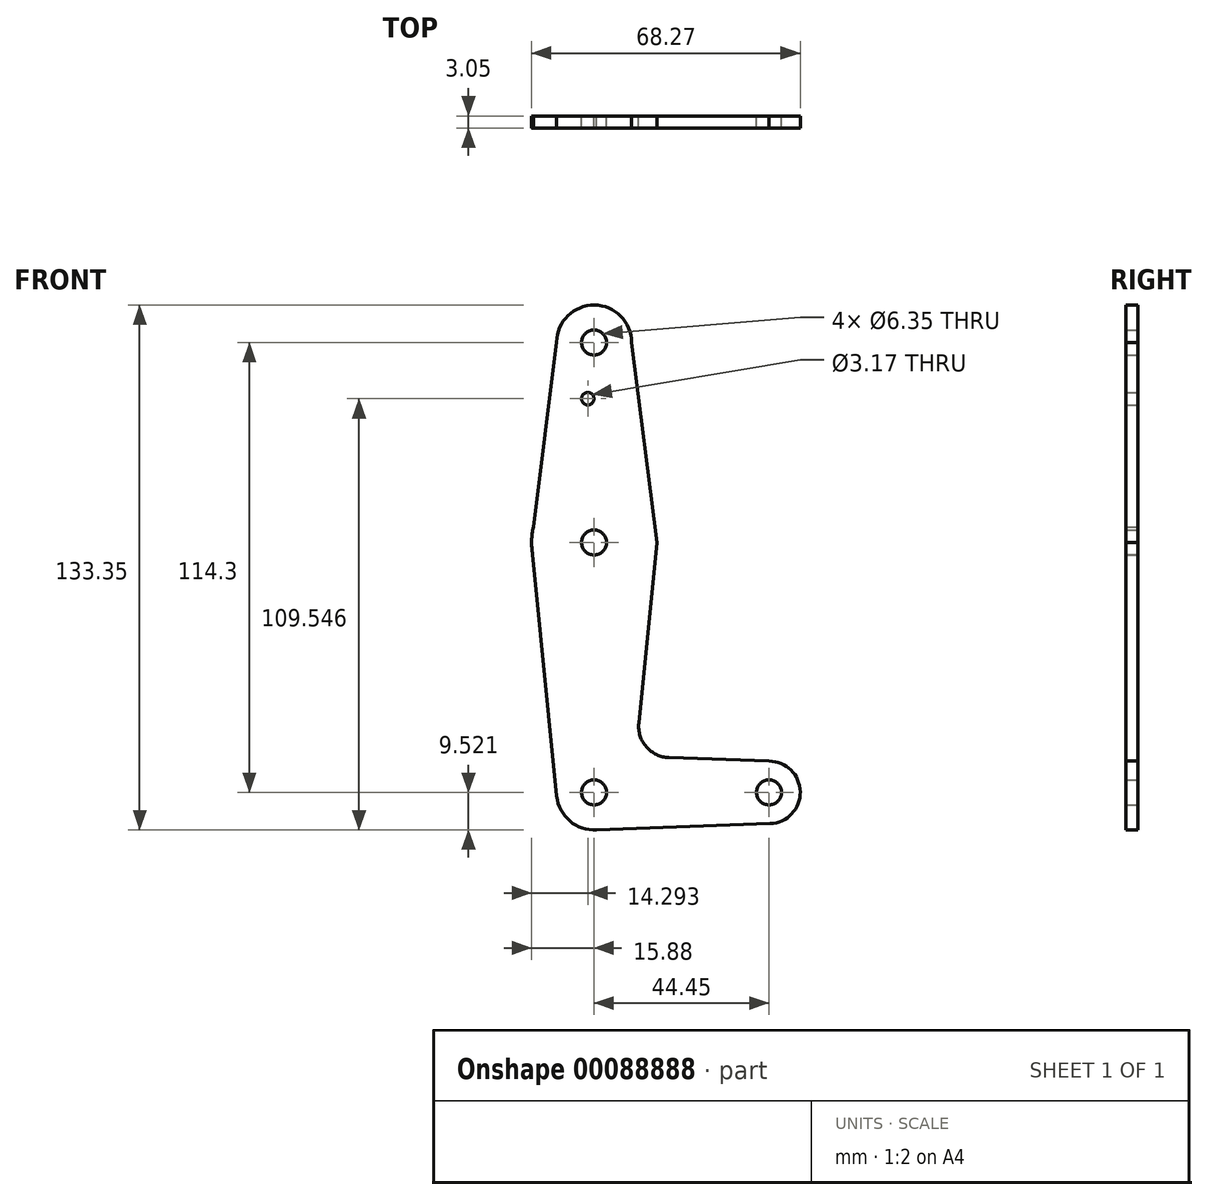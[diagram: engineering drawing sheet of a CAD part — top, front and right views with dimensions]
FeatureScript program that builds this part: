
annotation { "Feature Type Name" : "Feature", "Feature Type Description" : "" }
export const myFeature = defineFeature(function(context is Context, id is Id, definition is map)
    precondition{}
    {
        {
            var Q0;
            Q0=qCreatedBy(makeId("Front.planeOp"),FACE);
            var sketch = newSketch(context, id + "F0", { "sketchPlane" : qUnion([Q0])});
            skLineSegment(sketch, "E0", {"start": v(0, 89.5) * mm, "end": v(0, 38.7) * mm, "construction": true});
            skLineSegment(sketch, "E1", {"start": v(0, 38.7) * mm, "end": v(0, -24.8) * mm, "construction": true});
            skLineSegment(sketch, "E2", {"start": v(0, -24.8) * mm, "end": v(44.45, -24.8) * mm});
            skCircle(sketch, "E3", {"center": v(0, 89.5) * mm, "radius": 9.53 * mm});
            skCircle(sketch, "E4", {"center": v(0, 38.7) * mm, "radius": 15.88 * mm});
            skCircle(sketch, "E5", {"center": v(0, -24.8) * mm, "radius": 9.53 * mm});
            skCircle(sketch, "E6", {"center": v(44.45, -24.8) * mm, "radius": 7.94 * mm});
            skLineSegment(sketch, "E7", {"start": v(-9.52, 89.64) * mm, "end": v(-15.87, 38.63) * mm});
            skLineSegment(sketch, "E8", {"start": v(9.52, 89.5) * mm, "end": v(16.01, 38.63) * mm});
            skLineSegment(sketch, "E9", {"start": v(-15.87, 38.63) * mm, "end": v(-9.48, -25.74) * mm});
            skLineSegment(sketch, "E10", {"start": v(16.01, 38.63) * mm, "end": v(11.36, -7.2) * mm});
            skLineSegment(sketch, "E11", {"start": v(18.99, -15.95) * mm, "end": v(44.45, -16.86) * mm});
            skLineSegment(sketch, "E12", {"start": v(0, -34.32) * mm, "end": v(44.73, -32.73) * mm});
            skCircle(sketch, "E13", {"center": v(0, 89.5) * mm, "radius": 3.18 * mm});
            skCircle(sketch, "E14", {"center": v(0, 38.7) * mm, "radius": 3.18 * mm});
            skCircle(sketch, "E15", {"center": v(0, -24.8) * mm, "radius": 3.18 * mm});
            skCircle(sketch, "E16", {"center": v(44.45, -24.8) * mm, "radius": 3.18 * mm});
            skPoint(sketch, "E17.newPointB", {"position": v(0, -15.27) * mm});
            skArc(sketch, "E17.filletArc", {"start": v(11.36, -7.2) * mm, "mid": v(13.28, -13.23) * mm, "end": v(18.99, -15.95) * mm});
            skCircle(sketch, "E18", {"center": v(-1.59, 75.23) * mm, "radius": 1.59 * mm});
            skSolve(sketch);
        }
        {
            var Q0;
            Q0 = qSketchRegion(id + "F0", true);
            extrude(context, id + "F1", {"entities" : qUnion([Q0]), "depth" : 3.05 * mm});
        }
    });
